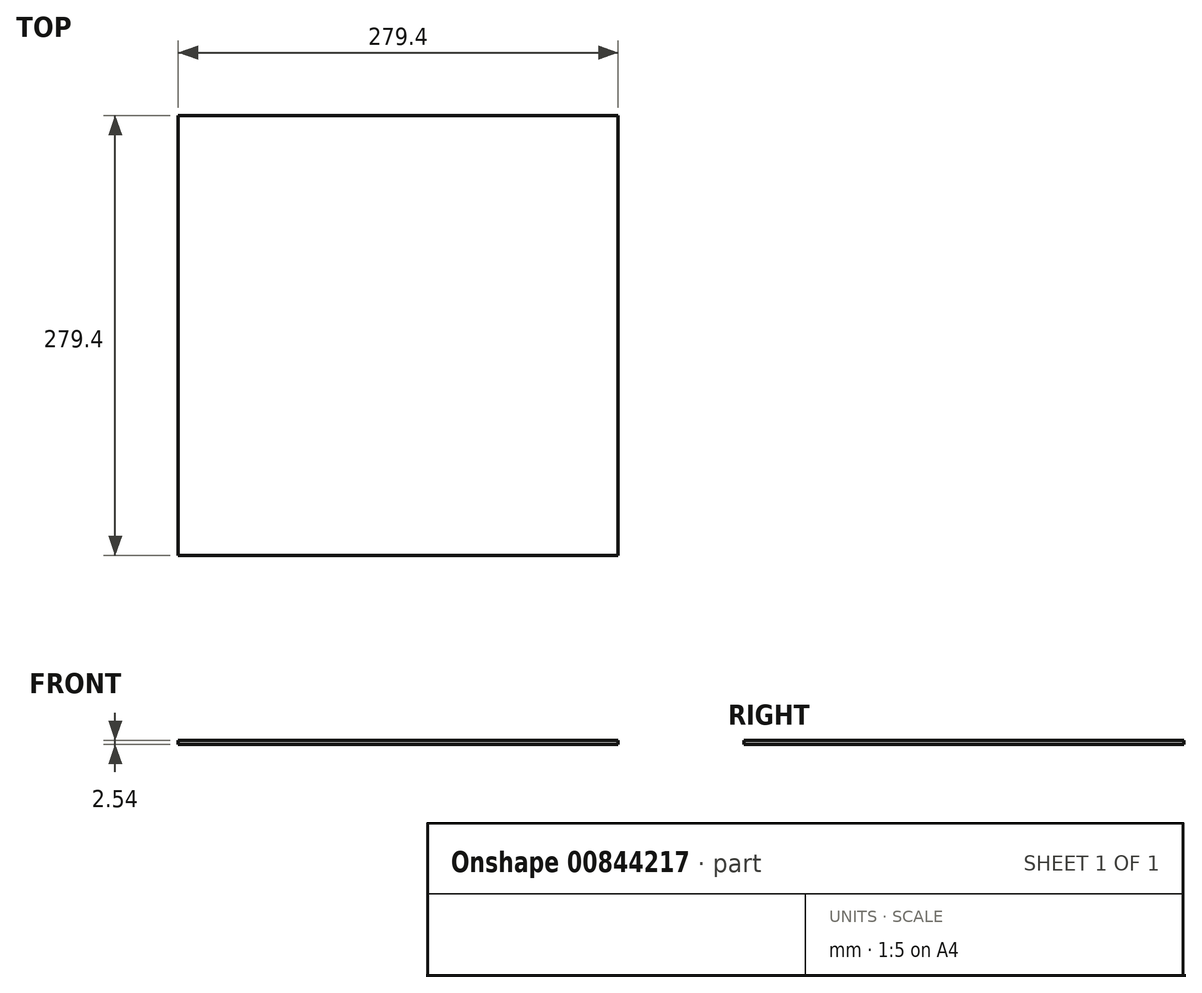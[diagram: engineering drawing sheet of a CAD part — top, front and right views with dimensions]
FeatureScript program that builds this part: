
annotation { "Feature Type Name" : "Feature", "Feature Type Description" : "" }
export const myFeature = defineFeature(function(context is Context, id is Id, definition is map)
    precondition{}
    {
        {
            var Q0;
            Q0=qCreatedBy(makeId("Top.planeOp"),FACE);
            var sketch = newSketch(context, id + "F0", { "sketchPlane" : qUnion([Q0])});
            skLineSegment(sketch, "E0.bottom", {"start": v(139.7, 139.7) * mm, "end": v(-139.7, 139.7) * mm});
            skLineSegment(sketch, "E0.top", {"start": v(139.7, -139.7) * mm, "end": v(-139.7, -139.7) * mm});
            skLineSegment(sketch, "E0.left", {"start": v(139.7, 139.7) * mm, "end": v(139.7, -139.7) * mm});
            skLineSegment(sketch, "E0.right", {"start": v(-139.7, 139.7) * mm, "end": v(-139.7, -139.7) * mm});
            skPoint(sketch, "E0.middle", {"position": v(0, 0) * mm});
            skSolve(sketch);
        }
        {
            var Q0;
            Q0=makeQuery(id+"F0.imprint","IMPRINT",FACE,{"disambiguationData":[TD([[makeQuery(id+"F0.imprint","IMPRINT",EDGE,{"derivedFrom":sQuery(id+"F0.wireOp",EDGE,"E0.bottom")}),1.0]])]});
            extrude(context, id + "F1", {"entities" : qUnion([Q0]), "depth" : 2.54 * mm, "offsetDistance" : 25.4 * mm});
        }
    });
